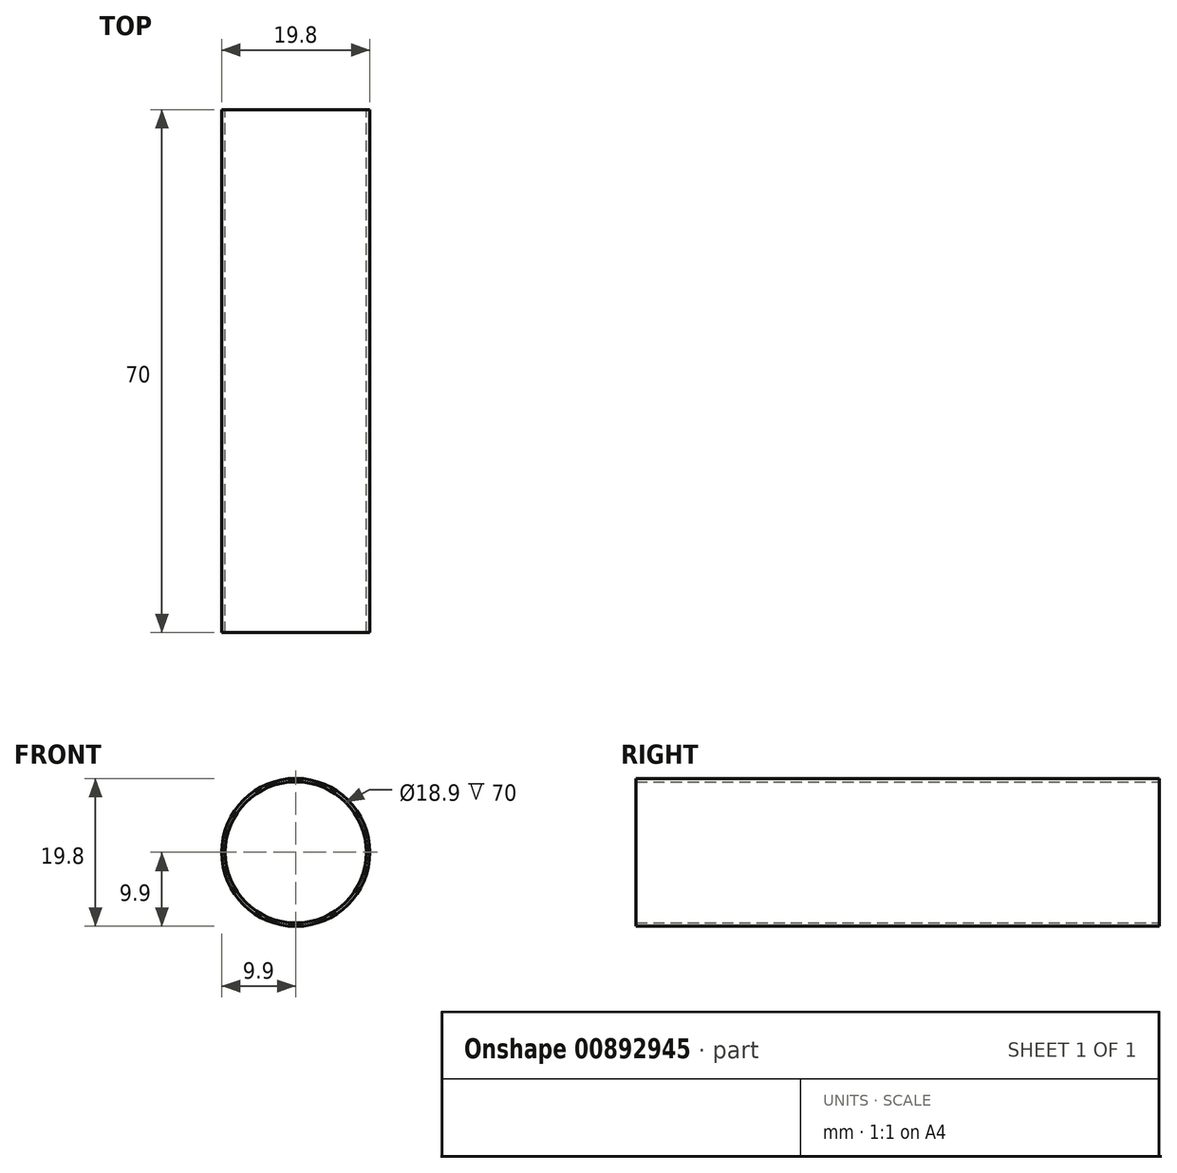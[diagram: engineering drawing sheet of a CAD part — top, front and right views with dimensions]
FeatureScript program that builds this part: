
annotation { "Feature Type Name" : "Feature", "Feature Type Description" : "" }
export const myFeature = defineFeature(function(context is Context, id is Id, definition is map)
    precondition{}
    {
        {
            var Q0;
            Q0=qCreatedBy(makeId("Front.planeOp"),FACE);
            var sketch = newSketch(context, id + "F0", { "sketchPlane" : qUnion([Q0])});
            skCircle(sketch, "E0", {"center": v(0, 0) * mm, "radius": 9.45 * mm});
            skCircle(sketch, "E1", {"center": v(0, 0) * mm, "radius": 9.9 * mm});
            skSolve(sketch);
        }
        {
            var Q0;
            Q0 = qSketchRegion(id + "F0", true);
            extrude(context, id + "F1", {"entities" : qUnion([Q0]), "depth" : 70 * mm, "offsetDistance" : 25 * mm});
        }
    });
